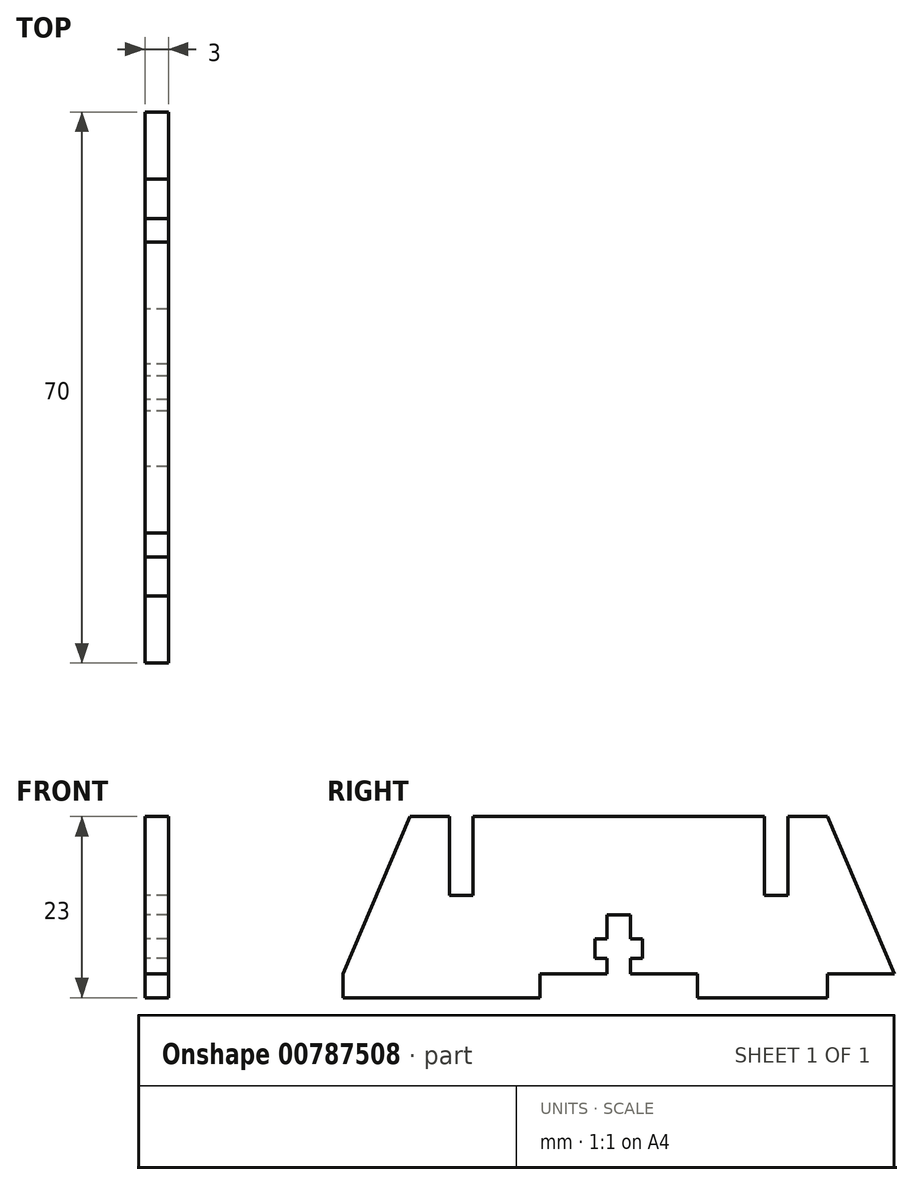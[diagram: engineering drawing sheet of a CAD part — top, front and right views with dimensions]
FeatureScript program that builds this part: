
annotation { "Feature Type Name" : "Feature", "Feature Type Description" : "" }
export const myFeature = defineFeature(function(context is Context, id is Id, definition is map)
    precondition{}
    {
        {
            var Q0;
            Q0=qCreatedBy(makeId("Right.planeOp"),FACE);
            var sketch = newSketch(context, id + "F0", { "sketchPlane" : qUnion([Q0])});
            skLineSegment(sketch, "E0", {"start": v(-11.5, 33.95) * mm, "end": v(-11.5, 23.95) * mm});
            skLineSegment(sketch, "E1", {"start": v(-11.5, 23.95) * mm, "end": v(-8.5, 23.95) * mm});
            skLineSegment(sketch, "E2", {"start": v(-8.5, 23.95) * mm, "end": v(-8.5, 33.95) * mm});
            skLineSegment(sketch, "E3", {"start": v(-8.5, 33.95) * mm, "end": v(28.5, 33.95) * mm});
            skLineSegment(sketch, "E4", {"start": v(28.5, 33.95) * mm, "end": v(28.5, 23.95) * mm});
            skLineSegment(sketch, "E5", {"start": v(28.5, 23.95) * mm, "end": v(31.5, 23.95) * mm});
            skLineSegment(sketch, "E6", {"start": v(31.5, 23.95) * mm, "end": v(31.5, 33.95) * mm});
            skLineSegment(sketch, "E7", {"start": v(31.5, 33.95) * mm, "end": v(36.5, 33.95) * mm});
            skLineSegment(sketch, "E8", {"start": v(36.5, 33.95) * mm, "end": v(45, 13.95) * mm});
            skLineSegment(sketch, "E9", {"start": v(-25, 13.95) * mm, "end": v(-16.5, 33.95) * mm});
            skLineSegment(sketch, "E10", {"start": v(-16.5, 33.95) * mm, "end": v(-11.5, 33.95) * mm});
            skLineSegment(sketch, "E11", {"start": v(-25, 13.95) * mm, "end": v(-25, 10.95) * mm});
            skLineSegment(sketch, "E12", {"start": v(-25, 10.95) * mm, "end": v(0, 10.95) * mm});
            skLineSegment(sketch, "E13", {"start": v(45, 10.95) * mm, "end": v(45, 13.95) * mm});
            skPoint(sketch, "E14", {"position": v(-10, 23.95) * mm});
            skPoint(sketch, "E15", {"position": v(30, 23.95) * mm});
            skPoint(sketch, "E16", {"position": v(10, 33.95) * mm});
            skLineSegment(sketch, "E17", {"start": v(0, 10.95) * mm, "end": v(0, 13.95) * mm});
            skLineSegment(sketch, "E18", {"start": v(0, 13.95) * mm, "end": v(20, 13.95) * mm});
            skLineSegment(sketch, "E19", {"start": v(20, 13.95) * mm, "end": v(20, 10.95) * mm});
            skPoint(sketch, "E20", {"position": v(10, 13.95) * mm});
            skLineSegment(sketch, "E21.trimOffspring", {"start": v(20, 10.95) * mm, "end": v(45, 10.95) * mm});
            skLineSegment(sketch, "E22", {"start": v(10, 33.95) * mm, "end": v(10, 13.95) * mm, "construction": true});
            skLineSegment(sketch, "E23.bottom", {"start": v(8.5, 13.95) * mm, "end": v(11.5, 13.95) * mm});
            skLineSegment(sketch, "E23.top", {"start": v(8.5, 21.45) * mm, "end": v(11.5, 21.45) * mm});
            skLineSegment(sketch, "E23.left", {"start": v(8.5, 13.95) * mm, "end": v(8.5, 21.45) * mm});
            skLineSegment(sketch, "E23.right", {"start": v(11.5, 13.95) * mm, "end": v(11.5, 21.45) * mm});
            skPoint(sketch, "E23.middle", {"position": v(10, 17.7) * mm});
            skLineSegment(sketch, "E24.bottom", {"start": v(7, 15.95) * mm, "end": v(13, 15.95) * mm});
            skLineSegment(sketch, "E24.top", {"start": v(7, 18.45) * mm, "end": v(13, 18.45) * mm});
            skLineSegment(sketch, "E24.left", {"start": v(7, 15.95) * mm, "end": v(7, 18.45) * mm});
            skLineSegment(sketch, "E24.right", {"start": v(13, 15.95) * mm, "end": v(13, 18.45) * mm});
            skPoint(sketch, "E24.middle", {"position": v(10, 17.2) * mm});
            skLineSegment(sketch, "E25", {"start": v(45, 13.95) * mm, "end": v(36.5, 13.95) * mm});
            skLineSegment(sketch, "E26", {"start": v(36.5, 13.95) * mm, "end": v(36.5, 10.95) * mm});
            skSolve(sketch);
        }
        {
            var Q0;
            Q0=makeQuery(id+"F0.imprint","IMPRINT",FACE,{"disambiguationData":[TD([[makeQuery(id+"F0.imprint","IMPRINT",EDGE,{"derivedFrom":sQuery(id+"F0.wireOp",EDGE,"E0")}),-1.0]])]});
            extrude(context, id + "F1", {"entities" : qUnion([Q0]), "depth" : 3 * mm, "offsetDistance" : 25.4 * mm});
        }
    });
